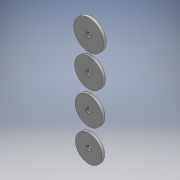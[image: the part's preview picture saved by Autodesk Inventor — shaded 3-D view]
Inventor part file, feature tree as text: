
AUTODESK INVENTOR PART (.ipt)
format: ipt  version: 2016 (Build 200138000, 138)  size: 126,464 bytes
history: native  units: mm
features: extrude x1, sketch x1
ambient origin geometry x8: Origin, YZ Plane, XZ Plane, XY Plane, X Axis, Y Axis, Z Axis, Center Point
bodies: Solid1 (feature_tree)
feature tree (2):
  extrude  "Extrusion1"  Depth=3.195mm
  sketch  "Sketch1"  dims[d6=6.35mm d10=36.400485mm d24=6.35mm d25=34.48467mm d27=6.35mm d29=33.335181mm d35=6.35mm d36=32.568855mm d43=40.0mm d44=40.0mm d45=40.0mm d46=3.195mm d47=0.0mm]
